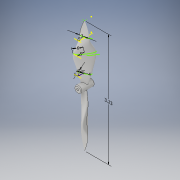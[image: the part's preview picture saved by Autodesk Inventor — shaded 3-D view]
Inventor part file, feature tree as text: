
AUTODESK INVENTOR PART (.ipt)
format: ipt  version: 2018 (Build 220112000, 112)  size: 265,728 bytes
history: native  units: in
note: dims shown in document units (in); Inventor stores cm internally (conversion verified against a paired STEP export)
features: plane x8, sketch x8, other x2, extrude x1, loft x1, pattern_circular x1, fillet x1
ambient origin geometry x8: Origin, YZ Plane, XZ Plane, XY Plane, X Axis, Y Axis, Z Axis, Center Point
bodies: Solid1 (feature_tree)
feature tree (22):
  other  "Annotations"
  extrude  "Extrusion1"  Depth=0.0591in
  plane  "Work Plane1"
  plane  "Work Plane2"
  plane  "Work Plane3"
  sketch  "Sketch29"  dims[d0=0.1969in d1=0.0591in]
  plane  "Work Plane7"
  sketch  "Sketch30"  dims[d2=0.3937in d3=0.0in d141=0.0394in]
  plane  "Work Plane8"
  sketch  "Sketch31"  dims[d142=0.0787in]
  plane  "Work Plane11"
  sketch  "Sketch33"  dims[d143=0.0394in]
  plane  "Work Plane12"
  sketch  "Sketch34"  dims[d144=0.1969in]
  plane  "Work Plane13"
  loft  "Loft1"
  pattern_circular  "Circular Pattern1"  [2 undecoded]
  fillet  "Fillet8"  Radius=0.3937in
  sketch  "Sketch36"  dims[d146=0.0472in]
  sketch  "Sketch - Propeller Connecter"  dims[d147=0.1575in d150=0.4921in d151=0.3937in d152=0.3937in d153=0.1969in d154=0.1969in d155=0.0in d156=90.0deg d157=0.0in d158=90.0deg d159=0.0in d160=90.0deg d161=0.0in d162=90.0deg d163=0.0in d164=90.0deg d165=0.7874in d166=360.0deg d168=0.2362in d169=0.0197in d171=0.1181in d170=3.2283in]
  sketch  "Sketch35"  dims[d145=0.2953in]
  other  "Linear Dimension 1"
note: 2 required parameter values undecoded (feature->parameter linkage not recoverable at this tier; creation-order binding heuristic only, values carry confidence <= 0.55)
